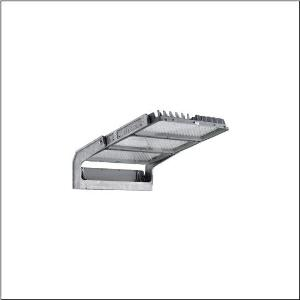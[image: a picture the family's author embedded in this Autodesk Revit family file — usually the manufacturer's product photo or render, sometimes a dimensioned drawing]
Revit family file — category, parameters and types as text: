
# Revit family: floodlight_fl_11_maxi_pro___rs07_5xa779124k01gb_d181
name_source: partatom
category: Lighting Fixtures
units: mm (PartAtom-declared; Revit-internal decimal feet)

## family parameters
Cut with Voids When Loaded = No
Host = Face
Light Source = No
Part Type = Normal
Room Calculation Point = No
Round Connector Dimension = Use Diameter
Shared = No

## types (1)
- --- (1 x LED, 123000 lm, 1227.1 W, 5700K)
    Apparent Load = 1227 VA
    CIE Flux Codes = 80 93 99 100 99
    Color Rendering = 90
    Color Temperature = 5700K
    Default Elevation = 1800 mm
    Description = Floodlight FL 11  maxi  pro floodlight; light control with lens of PMMA; cover panel of toughened safety glass, transparent; light distribution: RS07, rotationally symmetric direct distribution, LED; colour temperature: 5700K, rated luminous flux: 123.000lm, colour rendering: CRI > 90, light colour: 957; luminous efficacy: 100lm/W; brightness control: DALI 2; with terminal, 5-pole, max. 2.5mm², mains connection: 220..240V/380..400V AC, 50/60Hz, surge voltage resistance: line to ground: 10kV, LED service life up to 100,000h L90. Typical operating time: 1000h per year., ECG replaceable separately, LED unit replaceable without ESD environment, dustproof LED module, dimming range 10..100%; 1227W floodlight with 3x LED unit of diecast aluminium, coated grey; length: 1.003mm / width: 651mm / height: 338mm; mounting bracket, of diecast aluminium, uncoated, natural, equipment: Power, protection rating (complete): IP66; insulation class (complete): insulation class I (protective earthing); certification: CE, ENEC, VDE; ball protection: ball impact resistant, only for outdoor installations in the designated locations, permissible operating ambient temperature: -45..+55°C, permissible storage temperature: -40..+85°Cpackaging unit: 1 piece

Light Distribution: RS07
    Height = 320 mm
    Lamp = 1 x LED
    Lamp Light Flux = 123000 lm
    Lamp Power = 1227.1 W
    Lamp count = 1
    Length = 1002 mm
    Luminous efficacy = 100 lm/W
    Manufacturer = Siteco
    ModVariant = No
    Model = 5XA779124K01GB
    Mounting Place = Ceiling
    Mounting Type = Surface mounted
    Number of Poles = 1
    OnlyDefault = Yes
    Power Factor = 1
    Product Name = Floodlight FL 11 maxi pro | RS07
    Product group = floodlight | ceiling mounted
    ProductGroupID = 303
    Protection Class = Protection class I
    Protection Degree = IP 66
    RLX_Detail_Level = 1
    RLX_Emergency_Light_Flux = 0 lm
    RLX_Emergency_Type = 0
    RLX_Emergency_Type_DB = No
    RlxData = <blob elided: 40277 chars, md5=d747732a>
    Socket = socket
    Standby Power = 0 W
    System Light Flux = 123000 lm
    System Power = 1227 W
    Type Comments = factory setting: luminous flux: 100 % | dim-lin: 254 | 840 mA
    Type Image = l_1356210.jpg
    URL = http://relux.com
    VarID = @adj_039053
    Voltage = 0 V
    Weight = 0.00 kg
    Width = 655 mm

## geometry (parser evidence)
native form markers: Blend x4, Sweep x14
no freeform markers — native parametric forms only
